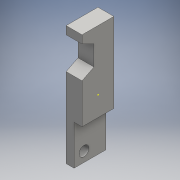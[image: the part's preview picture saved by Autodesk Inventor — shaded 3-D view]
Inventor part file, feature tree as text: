
AUTODESK INVENTOR PART (.ipt)
format: ipt  version: 2016 (Build 200138000, 138)  size: 122,368 bytes
history: native  units: mm
features: sketch x5, extrude x4, other x1
ambient origin geometry x8: Origin, YZ Plane, XZ Plane, XY Plane, X Axis, Y Axis, Z Axis, Center Point
bodies: Body1 (feature_tree)
feature tree (10):
  other  "ソリッド1"
  extrude  "押し出し1"  Depth=4.0mm
  extrude  "押し出し2"  Depth=30.0mm
  extrude  "押し出し6"  Depth=8.0mm TaperAngle=0.0deg
  extrude  "押し出し7"  Depth=5.0mm
  sketch  "スケッチ8"
  sketch  "スケッチ1"
  sketch  "スケッチ2"
  sketch  "スケッチ6"
  sketch  "スケッチ7"
